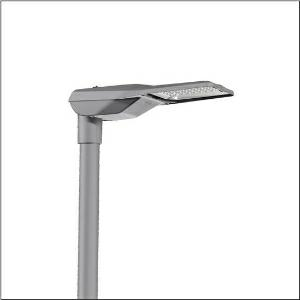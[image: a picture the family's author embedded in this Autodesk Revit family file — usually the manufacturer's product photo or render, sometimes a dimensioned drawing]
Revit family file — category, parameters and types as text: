
# Revit family: streetlight_sl_21_iq_mini___p0_8ab_5xe2r31v08jb_ae49
name_source: partatom
category: Lighting Fixtures
units: mm (PartAtom-declared; Revit-internal decimal feet)

## family parameters
Cut with Voids When Loaded = No
Host = Face
Light Source = No
Part Type = Normal
Room Calculation Point = No
Round Connector Dimension = Use Diameter
Shared = No

## types (1)
- --- (1 x LED, 9740 lm, 72.5 W, 3000K)
    Apparent Load = 73 VA
    CIE Flux Codes = 39 72 97 100 100
    Color Rendering = 70
    Color Temperature = 3000K
    Default Elevation = 1800 mm
    Description = Streetlight SL 21 iQ mini, mast luminaire, primary light control with lens, of PMMA, primary optical cover: cover, of toughened safety glass, transparent, light distribution: P0.8aB, light emission: direct distribution, primary light characteristic: asymmetric, installation type: post-top, side-entry, LED, High Power LED, rated luminous flux: 9.740lm, luminous efficacy: 134lm/W, light colour: 730, colour temperature: 3000K, control gear: iQ-Street Remote, D4i with power reduction, control: pre-setting: logarithmic dimming characteristic, Street-Remote, Auto-Match, Temp-Guard, Lumen-Switch, Night-Set, Smart-Wire, Light-Fading, Desk-Remote (wireless, voltage-free reading and setting of iQ features in the workshop via application-optimized NFC function/RFID function), optimised constant luminous flux control (CLO 2.0), mains connection: 220..240V, AC, 50/60Hz, start of lifetime: 73W, end of service life: 76W, reduction: 33W, luminaire housing, of diecast aluminium, powder-coated, Siteco® metallic grey (DB 702S), corrosivity category C5 mid according to DIN EN ISO 12944, please order mast flange separately, inclination adjustable: 0°, 5°, 10°, 15°, sealing non-destructively replaceable, multi-level sealing system, length: 628mm, width: 235mm, height: 110mm, mast flange for spigot size: 42mm (side-entry): 5XC10008XM4, 60/48mm (side-entry/post-top): 5XC10108XM2, 76/60mm (side-entry/post-top): 5XC10108XM1, mounting height: 4..8m, Smart Interface above, protection rating (complete): IP66, insulation class (complete): insulation class II (safety insulation), certification: CE, ENEC, ENEC+, VDE, impact resistance: IK09, permissible operating ambient temperature for outdoor applications: -40..+50°C, standard-compliant lighting for roads and squares, packaging unit: 1 piece

Light Distribution: P0.8aB
    Height = 110 mm
    Lamp = 1 x LED
    Lamp Light Flux = 9740 lm
    Lamp Power = 72.5 W
    Lamp count = 1
    Length = 625 mm
    Luminous efficacy = 134 lm/W
    Manufacturer = Siteco
    ModVariant = No
    Model = 5XE2R31V08JB
    Number of Poles = 1
    OnlyDefault = Yes
    Power Factor = 1
    Product Name = Streetlight SL 21 iQ mini | P0.8aB
    Product group = mast luminaire | pylon top
    ProductGroupID = 6100
    Protection Class = Protection class II
    Protection Degree = IP 66
    RLX_Detail_Level = 1
    RLX_Emergency_Light_Flux = 0 lm
    RLX_Emergency_Type = 0
    RLX_Emergency_Type_DB = No
    RlxData = <blob elided: 92333 chars, md5=26164087>
    Socket = socket
    Standby Power = 0 W
    System Light Flux = 9740 lm
    System Power = 73 W
    Type Comments = factory setting: luminous flux: 100 % | dim-lin: 254 | 755 mA
    Type Image = l_1003515.jpg
    URL = http://relux.com
    VarID = @adj_068294
    Voltage = 0 V
    Weight = 0.00 kg
    Width = 234 mm

## geometry (parser evidence)
native form markers: Blend x4, Sweep x10
no freeform markers — native parametric forms only
